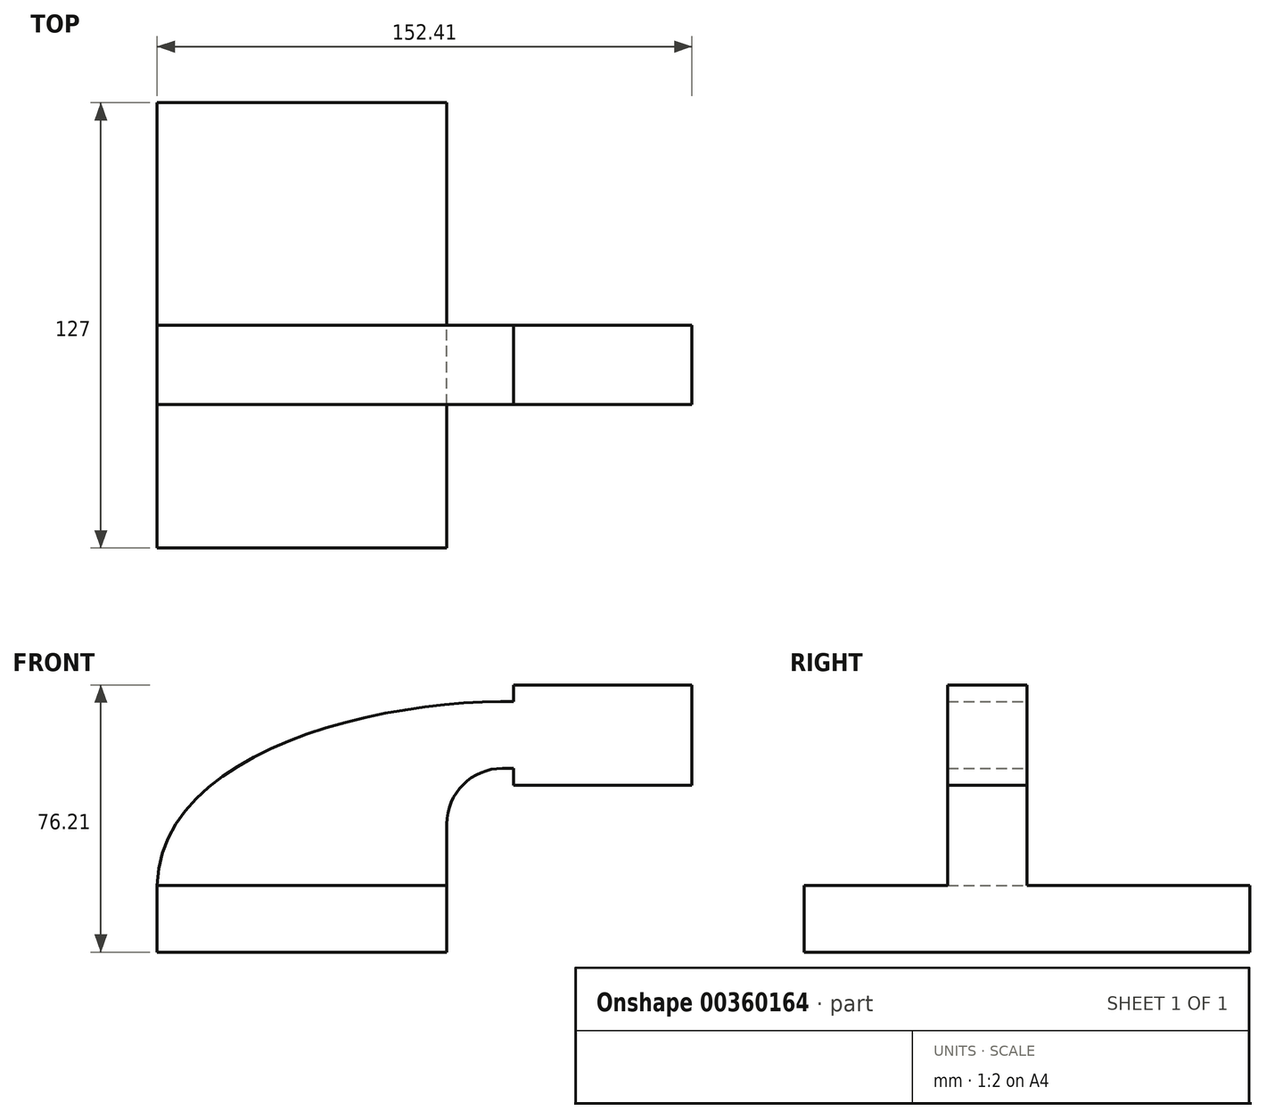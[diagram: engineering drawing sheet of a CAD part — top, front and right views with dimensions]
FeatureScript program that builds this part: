
annotation { "Feature Type Name" : "Feature", "Feature Type Description" : "" }
export const myFeature = defineFeature(function(context is Context, id is Id, definition is map)
    precondition{}
    {
        {
            var Q0;
            Q0=qCreatedBy(makeId("Front.planeOp"),FACE);
            var sketch = newSketch(context, id + "F0", { "sketchPlane" : qUnion([Q0])});
            skLineSegment(sketch, "E0.bottom", {"start": v(41.28, -9.52) * mm, "end": v(-41.28, -9.53) * mm});
            skLineSegment(sketch, "E0.top", {"start": v(41.28, 9.53) * mm, "end": v(-41.28, 9.53) * mm});
            skLineSegment(sketch, "E0.left", {"start": v(41.28, -9.52) * mm, "end": v(41.28, 9.53) * mm});
            skLineSegment(sketch, "E0.right", {"start": v(-41.28, -9.53) * mm, "end": v(-41.28, 9.53) * mm});
            skPoint(sketch, "E0.middle", {"position": v(0, 0) * mm});
            skLineSegment(sketch, "E1.bottom", {"start": v(111.12, 38.1) * mm, "end": v(60.32, 38.1) * mm});
            skLineSegment(sketch, "E1.top", {"start": v(111.12, 66.68) * mm, "end": v(60.32, 66.68) * mm});
            skLineSegment(sketch, "E1.left", {"start": v(111.12, 38.1) * mm, "end": v(111.12, 66.68) * mm});
            skLineSegment(sketch, "E1.right", {"start": v(60.32, 38.1) * mm, "end": v(60.32, 66.68) * mm});
            skPoint(sketch, "E1.middle", {"position": v(85.72, 52.39) * mm});
            skLineSegment(sketch, "E2", {"start": v(41.28, 9.53) * mm, "end": v(41.28, 27) * mm});
            skPoint(sketch, "E3.endSnap0", {"position": v(60.32, 52.39) * mm});
            skArc(sketch, "E4", {"start": v(41.27, 27) * mm, "mid": v(45.92, 38.23) * mm, "end": v(57.15, 42.88) * mm});
            skLineSegment(sketch, "E5", {"start": v(57.15, 42.88) * mm, "end": v(85.72, 42.88) * mm});
            skLineSegment(sketch, "E6.0", {"start": v(57.15, 61.93) * mm, "end": v(85.72, 61.93) * mm});
            skArc(sketch, "E6.1", {"start": v(22.23, 27) * mm, "mid": v(32.45, 51.7) * mm, "end": v(57.15, 61.93) * mm});
            skLineSegment(sketch, "E6.2", {"start": v(22.22, 9.53) * mm, "end": v(22.22, 27) * mm});
            skLineSegment(sketch, "E7", {"start": v(85.72, 38.1) * mm, "end": v(85.72, 66.68) * mm});
            skFitSpline(sketch, "E8", {"points": [v(-41.28, 9.52) * mm, v(57.15, 61.93) * mm], "startDerivative": vector(3.42, 112.4) * mm, "endDerivative": vector(116.17, 0.7) * mm});
            skSolve(sketch);
        }
        {
            var Q0;
            Q0=makeQuery(id+"F0.imprint","IMPRINT",FACE,{"disambiguationData":[TD([[makeQuery(id+"F0.imprint","IMPRINT",EDGE,{"derivedFrom":sQuery(id+"F0.wireOp",EDGE,"E0.bottom")}),-1.0]])]});
            extrude(context, id + "F1", {"entities" : qUnion([Q0]), "endBound" : BoundingType.SYMMETRIC, "depth" : 127 * mm});
        }
        {
            var Q0;
            Q0 = qSketchRegion(id + "F0", true);
            extrude(context, id + "F2", {"entities" : qUnion([Q0]), "operationType" : NewBodyOperationType.ADD, "depth" : 22.6 * mm});
        }
    });
